# Revit family: 57_CRD_ME_BKT_fan
name_source: partatom
category: Mechanical Equipment
units: mm (PartAtom-declared; Revit-internal decimal feet)

## family parameters
Always vertical = Yes
Cut with Voids When Loaded = No
OmniClass Number = 23.75.00.00
OmniClass Title = Climate Control (HVAC)
Part Type = Normal
Room Calculation Point = Yes
Round Connector Dimension = Use Diameter
Shared = No
Work Plane-Based = Yes

## types (1)
- BKT fan
    Default Elevation = 1219 mm
    IfcExportAs = IfcAirTerminalBoxType
    IfcExportType = NOTDEFINED
    Manufacturer = ClimaRad
    Model = BKT fan
    Power = 15 VA
    Voltage = 230 V
    breedte = 210 mm  [stored 0.688976 ft]
    diameter_terugslagklep = 98 mm  [stored 0.321522 ft]
    diepte = 122 mm  [stored 0.400262 ft]
    diepte_achterplaat = 10 mm  [stored 0.0328084 ft]
    diepte_terugslagklep = 53 mm  [stored 0.173885 ft]
    diepte_unit = 70 mm  [stored 0.229659 ft]
    hoogte = 210 mm  [stored 0.688976 ft]
    materiaal = <By Category>

note: [stored X ft] marks values corroborated as IEEE doubles in the binary element streams (Revit-internal decimal feet)

## geometry (parser evidence)
native form markers: Sweep x2
no freeform markers — native parametric forms only
